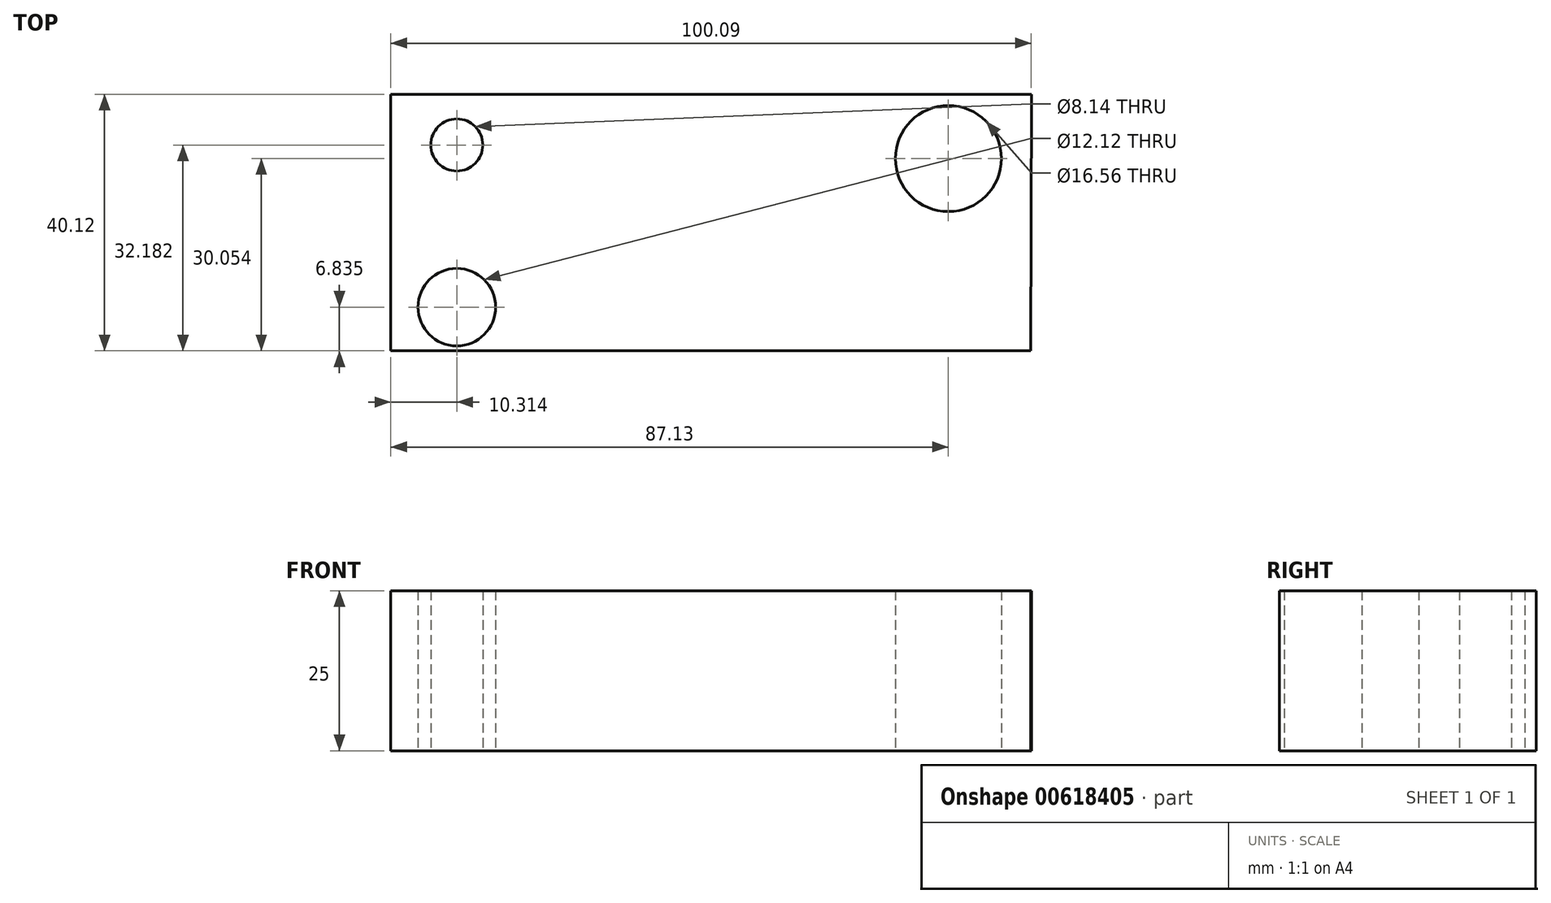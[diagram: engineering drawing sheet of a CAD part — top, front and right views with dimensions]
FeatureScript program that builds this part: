
annotation { "Feature Type Name" : "Feature", "Feature Type Description" : "" }
export const myFeature = defineFeature(function(context is Context, id is Id, definition is map)
    precondition{}
    {
        {
            var Q0;
            Q0=qCreatedBy(makeId("Top.planeOp"),FACE);
            var sketch = newSketch(context, id + "F0", { "sketchPlane" : qUnion([Q0])});
            skLineSegment(sketch, "E0", {"start": v(-89.39, -8.48) * mm, "end": v(10.61, -8.48) * mm});
            skLineSegment(sketch, "E1", {"start": v(-89.39, -8.48) * mm, "end": v(-89.39, 31.64) * mm});
            skLineSegment(sketch, "E2", {"start": v(-89.39, 31.64) * mm, "end": v(10.7, 31.64) * mm});
            skLineSegment(sketch, "E3", {"start": v(10.7, 31.64) * mm, "end": v(10.61, -8.48) * mm});
            skCircle(sketch, "E4", {"center": v(-79.08, 23.7) * mm, "radius": 4.07 * mm});
            skCircle(sketch, "E5", {"center": v(-79.08, -1.64) * mm, "radius": 6.06 * mm});
            skCircle(sketch, "E6", {"center": v(-2.26, 21.57) * mm, "radius": 8.28 * mm});
            skSolve(sketch);
        }
        {
            var Q0;
            Q0=makeQuery(id+"F0.imprint","IMPRINT",FACE,{"disambiguationData":[TD([[makeQuery(id+"F0.imprint","IMPRINT",EDGE,{"derivedFrom":sQuery(id+"F0.wireOp",EDGE,"E0")}),1.0]])]});
            extrude(context, id + "F1", {"entities" : qUnion([Q0]), "depth" : 25 * mm, "offsetDistance" : 25 * mm});
        }
    });
